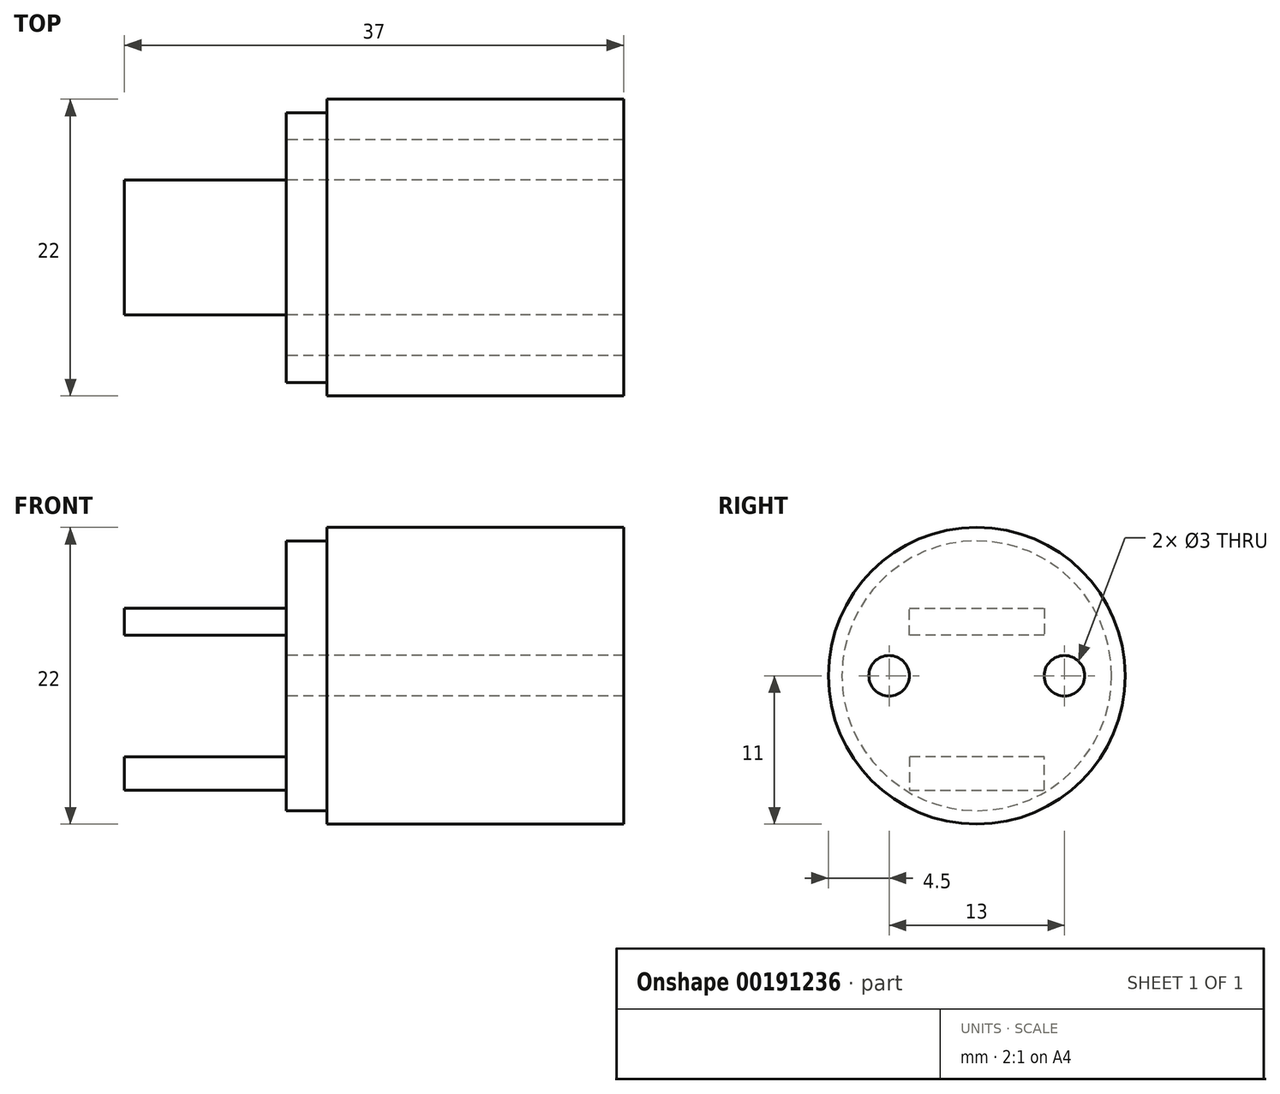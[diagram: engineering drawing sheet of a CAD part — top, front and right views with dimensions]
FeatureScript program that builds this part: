
annotation { "Feature Type Name" : "Feature", "Feature Type Description" : "" }
export const myFeature = defineFeature(function(context is Context, id is Id, definition is map)
    precondition{}
    {
        {
            var Q0;
            Q0=qCreatedBy(makeId("Right.planeOp"),FACE);
            var sketch = newSketch(context, id + "F0", { "sketchPlane" : qUnion([Q0])});
            skCircle(sketch, "E0", {"center": v(0, 0) * mm, "radius": 11 * mm});
            skCircle(sketch, "E1", {"center": v(6.5, 0) * mm, "radius": 1.5 * mm});
            skCircle(sketch, "E2", {"center": v(-6.5, 0) * mm, "radius": 1.5 * mm});
            skSolve(sketch);
        }
        {
            var Q0;
            Q0 = qSketchRegion(id + "F0", true);
            extrude(context, id + "F1", {"entities" : qUnion([Q0]), "depth" : 25 * mm});
        }
        {
            var Q0;
            Q0=makeQuery(id+"F1.opExtrude","CAP_FACE",FACE,{"disambiguationData":[OSD([sQuery(id+"F0.wireOp",EDGE,"E0")])],"isStart":true});
            var sketch = newSketch(context, id + "F2", { "sketchPlane" : qUnion([Q0])});
            skCircle(sketch, "E3", {"center": v(0, 0) * mm, "radius": 10 * mm});
            skCircle(sketch, "E4", {"center": v(0, 0) * mm, "radius": 12.5 * mm});
            skSolve(sketch);
        }
        {
            var Q0;
            Q0 = qSketchRegion(id + "F2", true);
            extrude(context, id + "F3", {"entities" : qUnion([Q0]), "operationType" : NewBodyOperationType.REMOVE, "oppositeDirection" : true, "depth" : 3 * mm});
        }
        {
            var Q0;
            Q0=makeQuery(id+"F1.opExtrude","CAP_FACE",FACE,{"disambiguationData":[OSD([sQuery(id+"F0.wireOp",EDGE,"E0")])],"isStart":true});
            var sketch = newSketch(context, id + "F4", { "sketchPlane" : qUnion([Q0])});
            skCircle(sketch, "E5", {"center": v(0, 0) * mm, "radius": 10 * mm, "construction": true});
            skLineSegment(sketch, "E6", {"start": v(-5, 11.3) * mm, "end": v(-5, -14.43) * mm, "construction": true});
            skLineSegment(sketch, "E7", {"start": v(5, 11.83) * mm, "end": v(5, -14.13) * mm, "construction": true});
            skLineSegment(sketch, "E8", {"start": v(-11.47, 3) * mm, "end": v(15.12, 3) * mm, "construction": true});
            skLineSegment(sketch, "E9", {"start": v(-13.3, -6) * mm, "end": v(15.17, -6) * mm, "construction": true});
            skLineSegment(sketch, "E10", {"start": v(-13.08, -8.5) * mm, "end": v(14.78, -8.5) * mm, "construction": true});
            skLineSegment(sketch, "E11", {"start": v(-11.9, 5) * mm, "end": v(16.18, 5) * mm, "construction": true});
            skLineSegment(sketch, "E12", {"start": v(-14.6, -5) * mm, "end": v(13.31, -5) * mm, "construction": true});
            skLineSegment(sketch, "E13", {"start": v(-14.43, -3) * mm, "end": v(12.68, -3) * mm, "construction": true});
            skLineSegment(sketch, "E14", {"start": v(-5, 5) * mm, "end": v(-5, 3) * mm});
            skLineSegment(sketch, "E15", {"start": v(-5, 3) * mm, "end": v(5, 3) * mm});
            skLineSegment(sketch, "E16", {"start": v(5, 3) * mm, "end": v(5, 5) * mm});
            skLineSegment(sketch, "E17", {"start": v(5, 5) * mm, "end": v(-5, 5) * mm});
            skLineSegment(sketch, "E18", {"start": v(-5, -6) * mm, "end": v(5, -6) * mm});
            skLineSegment(sketch, "E19", {"start": v(5, -6) * mm, "end": v(5, -8.5) * mm});
            skLineSegment(sketch, "E20", {"start": v(5, -8.5) * mm, "end": v(-5, -8.5) * mm});
            skLineSegment(sketch, "E21", {"start": v(-5, -8.5) * mm, "end": v(-5, -6) * mm});
            skSolve(sketch);
        }
        {
            var Q0;
            Q0 = qSketchRegion(id + "F4", true);
            extrude(context, id + "F5", {"entities" : qUnion([Q0]), "operationType" : NewBodyOperationType.ADD, "depth" : 12 * mm});
        }
    });
